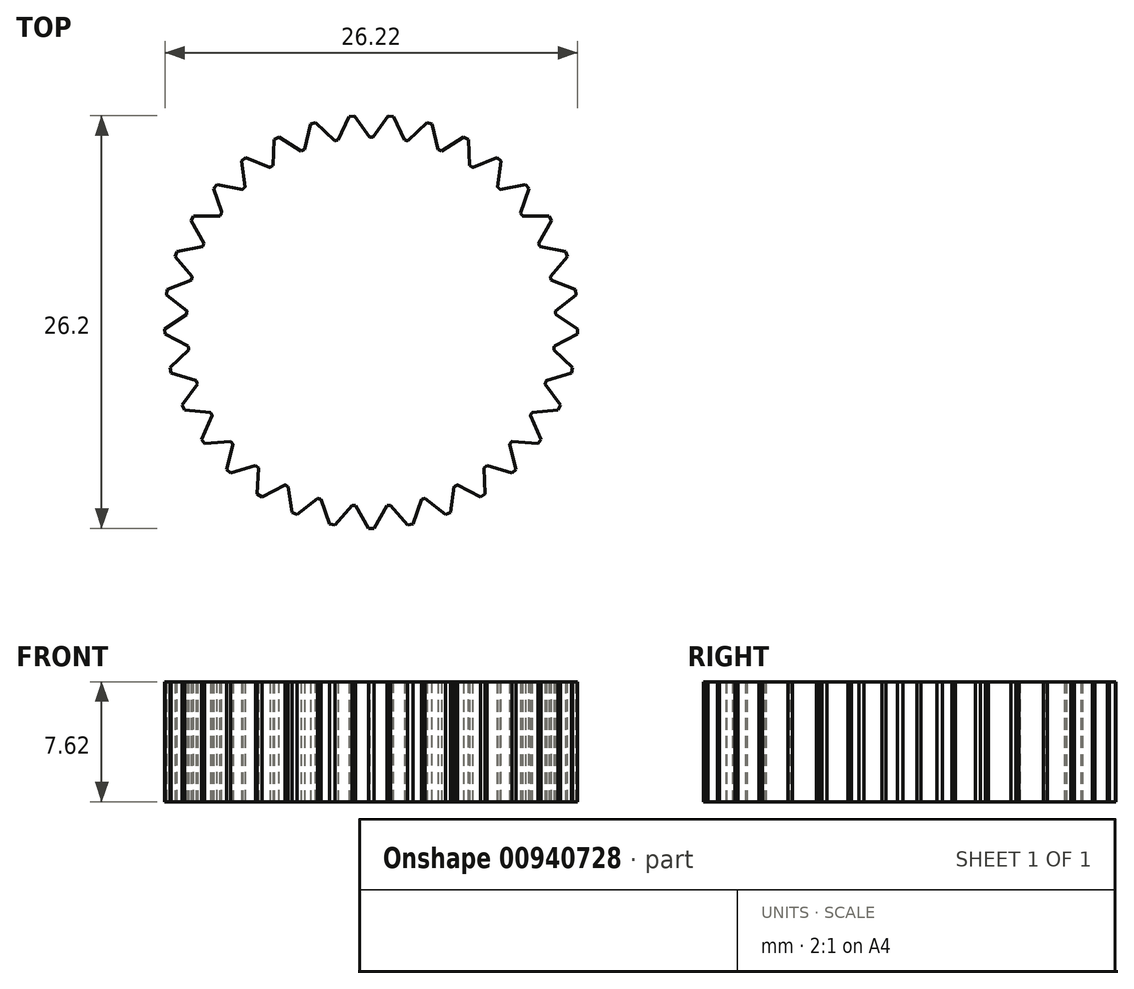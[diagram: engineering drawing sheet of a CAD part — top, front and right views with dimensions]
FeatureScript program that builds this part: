
annotation { "Feature Type Name" : "Feature", "Feature Type Description" : "" }
export const myFeature = defineFeature(function(context is Context, id is Id, definition is map)
    precondition{}
    {
        {
            var Q0;
            Q0=qCreatedBy(makeId("Top.planeOp"),FACE);
            var sketch = newSketch(context, id + "F0", { "sketchPlane" : qUnion([Q0])});
            skCircle(sketch, "E0", {"center": v(0, 0) * mm, "radius": 11.73 * mm});
            skSolve(sketch);
        }
        {
            var Q0;
            Q0 = qSketchRegion(id + "F0", true);
            extrude(context, id + "F1", {"entities" : qUnion([Q0]), "depth" : 7.62 * mm, "offsetDistance" : 25 * mm});
        }
        {
            var Q0;
            Q0=makeQuery(id+"F1.opExtrude","CAP_FACE",FACE,{"disambiguationData":[OSD([sQuery(id+"F0.wireOp",EDGE,"E0")])],"isStart":true});
            var sketch = newSketch(context, id + "F2", { "sketchPlane" : qUnion([Q0])});
            skCircle(sketch, "E1.cCircle", {"center": v(0, 12.26) * mm, "radius": 0.58 * mm, "construction": true});
            skLineSegment(sketch, "E1.0", {"start": v(1, 11.69) * mm, "end": v(-1, 11.69) * mm});
            skLineSegment(sketch, "E1.1", {"start": v(-1, 11.69) * mm, "end": v(0, 13.42) * mm});
            skLineSegment(sketch, "E1.2", {"start": v(0, 13.42) * mm, "end": v(1, 11.69) * mm});
            skPoint(sketch, "E1.0.midPoint", {"position": v(0, 11.69) * mm});
            skLineSegment(sketch, "E2.1.0", {"start": v(-3.2, 11.29) * mm, "end": v(-2.54, 13.18) * mm});
            skLineSegment(sketch, "E2.1.1", {"start": v(-2.54, 13.18) * mm, "end": v(-1.23, 11.66) * mm});
            skLineSegment(sketch, "E2.1.2", {"start": v(-1.23, 11.66) * mm, "end": v(-3.2, 11.29) * mm});
            skLineSegment(sketch, "E2.2.0", {"start": v(-5.27, 10.48) * mm, "end": v(-4.99, 12.46) * mm});
            skLineSegment(sketch, "E2.2.1", {"start": v(-4.99, 12.46) * mm, "end": v(-3.42, 11.22) * mm});
            skLineSegment(sketch, "E2.2.2", {"start": v(-3.42, 11.22) * mm, "end": v(-5.27, 10.48) * mm});
            skLineSegment(sketch, "E2.3.0", {"start": v(-7.16, 9.3) * mm, "end": v(-7.25, 11.29) * mm});
            skLineSegment(sketch, "E2.3.1", {"start": v(-7.25, 11.29) * mm, "end": v(-5.48, 10.37) * mm});
            skLineSegment(sketch, "E2.3.2", {"start": v(-5.48, 10.37) * mm, "end": v(-7.16, 9.3) * mm});
            skLineSegment(sketch, "E2.4.0", {"start": v(-8.79, 7.77) * mm, "end": v(-9.26, 9.71) * mm});
            skLineSegment(sketch, "E2.4.1", {"start": v(-9.26, 9.71) * mm, "end": v(-7.34, 9.15) * mm});
            skLineSegment(sketch, "E2.4.2", {"start": v(-7.34, 9.15) * mm, "end": v(-8.79, 7.77) * mm});
            skLineSegment(sketch, "E2.5.0", {"start": v(-10.1, 5.96) * mm, "end": v(-10.93, 7.78) * mm});
            skLineSegment(sketch, "E2.5.1", {"start": v(-10.93, 7.78) * mm, "end": v(-8.94, 7.6) * mm});
            skLineSegment(sketch, "E2.5.2", {"start": v(-8.94, 7.6) * mm, "end": v(-10.1, 5.96) * mm});
            skLineSegment(sketch, "E2.6.0", {"start": v(-11.05, 3.95) * mm, "end": v(-12.2, 5.57) * mm});
            skLineSegment(sketch, "E2.6.1", {"start": v(-12.2, 5.57) * mm, "end": v(-10.22, 5.76) * mm});
            skLineSegment(sketch, "E2.6.2", {"start": v(-10.22, 5.76) * mm, "end": v(-11.05, 3.95) * mm});
            skLineSegment(sketch, "E2.7.0", {"start": v(-11.6, 1.78) * mm, "end": v(-13.04, 3.16) * mm});
            skLineSegment(sketch, "E2.7.1", {"start": v(-13.04, 3.16) * mm, "end": v(-11.12, 3.73) * mm});
            skLineSegment(sketch, "E2.7.2", {"start": v(-11.12, 3.73) * mm, "end": v(-11.6, 1.78) * mm});
            skLineSegment(sketch, "E2.8.0", {"start": v(-11.72, -0.44) * mm, "end": v(-13.4, 0.64) * mm});
            skLineSegment(sketch, "E2.8.1", {"start": v(-13.4, 0.64) * mm, "end": v(-11.63, 1.55) * mm});
            skLineSegment(sketch, "E2.8.2", {"start": v(-11.63, 1.55) * mm, "end": v(-11.72, -0.44) * mm});
            skLineSegment(sketch, "E2.9.0", {"start": v(-11.43, -2.65) * mm, "end": v(-13.28, -1.9) * mm});
            skLineSegment(sketch, "E2.9.1", {"start": v(-13.28, -1.9) * mm, "end": v(-11.7, -0.67) * mm});
            skLineSegment(sketch, "E2.9.2", {"start": v(-11.7, -0.67) * mm, "end": v(-11.43, -2.65) * mm});
            skLineSegment(sketch, "E2.10.0", {"start": v(-10.72, -4.77) * mm, "end": v(-12.68, -4.39) * mm});
            skLineSegment(sketch, "E2.10.1", {"start": v(-12.68, -4.39) * mm, "end": v(-11.37, -2.88) * mm});
            skLineSegment(sketch, "E2.10.2", {"start": v(-11.37, -2.88) * mm, "end": v(-10.72, -4.77) * mm});
            skLineSegment(sketch, "E2.11.0", {"start": v(-9.62, -6.7) * mm, "end": v(-11.62, -6.7) * mm});
            skLineSegment(sketch, "E2.11.1", {"start": v(-11.62, -6.7) * mm, "end": v(-10.62, -4.98) * mm});
            skLineSegment(sketch, "E2.11.2", {"start": v(-10.62, -4.98) * mm, "end": v(-9.62, -6.7) * mm});
            skLineSegment(sketch, "E2.12.0", {"start": v(-8.18, -8.4) * mm, "end": v(-10.14, -8.79) * mm});
            skLineSegment(sketch, "E2.12.1", {"start": v(-10.14, -8.79) * mm, "end": v(-9.49, -6.9) * mm});
            skLineSegment(sketch, "E2.12.2", {"start": v(-9.49, -6.9) * mm, "end": v(-8.18, -8.4) * mm});
            skLineSegment(sketch, "E2.13.0", {"start": v(-6.44, -9.8) * mm, "end": v(-8.3, -10.55) * mm});
            skLineSegment(sketch, "E2.13.1", {"start": v(-8.3, -10.55) * mm, "end": v(-8.01, -8.57) * mm});
            skLineSegment(sketch, "E2.13.2", {"start": v(-8.01, -8.57) * mm, "end": v(-6.44, -9.8) * mm});
            skLineSegment(sketch, "E2.14.0", {"start": v(-4.47, -10.85) * mm, "end": v(-6.15, -11.93) * mm});
            skLineSegment(sketch, "E2.14.1", {"start": v(-6.15, -11.93) * mm, "end": v(-6.24, -9.93) * mm});
            skLineSegment(sketch, "E2.14.2", {"start": v(-6.24, -9.93) * mm, "end": v(-4.47, -10.85) * mm});
            skLineSegment(sketch, "E2.15.0", {"start": v(-2.33, -11.5) * mm, "end": v(-3.78, -12.88) * mm});
            skLineSegment(sketch, "E2.15.1", {"start": v(-3.78, -12.88) * mm, "end": v(-4.25, -10.93) * mm});
            skLineSegment(sketch, "E2.15.2", {"start": v(-4.25, -10.93) * mm, "end": v(-2.33, -11.5) * mm});
            skLineSegment(sketch, "E2.16.0", {"start": v(-0.12, -11.73) * mm, "end": v(-1.28, -13.36) * mm});
            skLineSegment(sketch, "E2.16.1", {"start": v(-1.28, -13.36) * mm, "end": v(-2.1, -11.54) * mm});
            skLineSegment(sketch, "E2.16.2", {"start": v(-2.1, -11.54) * mm, "end": v(-0.12, -11.73) * mm});
            skLineSegment(sketch, "E2.17.0", {"start": v(2.1, -11.54) * mm, "end": v(1.28, -13.36) * mm});
            skLineSegment(sketch, "E2.17.1", {"start": v(1.28, -13.36) * mm, "end": v(0.12, -11.73) * mm});
            skLineSegment(sketch, "E2.17.2", {"start": v(0.12, -11.73) * mm, "end": v(2.1, -11.54) * mm});
            skLineSegment(sketch, "E2.18.0", {"start": v(4.25, -10.93) * mm, "end": v(3.78, -12.88) * mm});
            skLineSegment(sketch, "E2.18.1", {"start": v(3.78, -12.88) * mm, "end": v(2.33, -11.5) * mm});
            skLineSegment(sketch, "E2.18.2", {"start": v(2.33, -11.5) * mm, "end": v(4.25, -10.93) * mm});
            skLineSegment(sketch, "E2.19.0", {"start": v(6.24, -9.93) * mm, "end": v(6.15, -11.93) * mm});
            skLineSegment(sketch, "E2.19.1", {"start": v(6.15, -11.93) * mm, "end": v(4.47, -10.85) * mm});
            skLineSegment(sketch, "E2.19.2", {"start": v(4.47, -10.85) * mm, "end": v(6.24, -9.93) * mm});
            skLineSegment(sketch, "E2.20.0", {"start": v(8.01, -8.57) * mm, "end": v(8.3, -10.55) * mm});
            skLineSegment(sketch, "E2.20.1", {"start": v(8.3, -10.55) * mm, "end": v(6.44, -9.8) * mm});
            skLineSegment(sketch, "E2.20.2", {"start": v(6.44, -9.8) * mm, "end": v(8.01, -8.57) * mm});
            skLineSegment(sketch, "E2.21.0", {"start": v(9.49, -6.9) * mm, "end": v(10.14, -8.79) * mm});
            skLineSegment(sketch, "E2.21.1", {"start": v(10.14, -8.79) * mm, "end": v(8.18, -8.4) * mm});
            skLineSegment(sketch, "E2.21.2", {"start": v(8.18, -8.4) * mm, "end": v(9.49, -6.9) * mm});
            skLineSegment(sketch, "E2.22.0", {"start": v(10.62, -4.98) * mm, "end": v(11.62, -6.7) * mm});
            skLineSegment(sketch, "E2.22.1", {"start": v(11.62, -6.7) * mm, "end": v(9.62, -6.7) * mm});
            skLineSegment(sketch, "E2.22.2", {"start": v(9.62, -6.7) * mm, "end": v(10.62, -4.98) * mm});
            skLineSegment(sketch, "E2.23.0", {"start": v(11.37, -2.88) * mm, "end": v(12.68, -4.39) * mm});
            skLineSegment(sketch, "E2.23.1", {"start": v(12.68, -4.39) * mm, "end": v(10.72, -4.77) * mm});
            skLineSegment(sketch, "E2.23.2", {"start": v(10.72, -4.77) * mm, "end": v(11.37, -2.88) * mm});
            skPoint(sketch, "E2.center", {"position": v(0, 0) * mm});
            skLineSegment(sketch, "E3.1.24.0", {"start": v(11.7, -0.67) * mm, "end": v(13.28, -1.9) * mm});
            skLineSegment(sketch, "E3.3.24.0", {"start": v(13.28, -1.9) * mm, "end": v(11.43, -2.65) * mm});
            skLineSegment(sketch, "E3.6.24.0", {"start": v(11.43, -2.65) * mm, "end": v(11.7, -0.67) * mm});
            skLineSegment(sketch, "E3.1.25.0", {"start": v(11.63, 1.55) * mm, "end": v(13.4, 0.64) * mm});
            skLineSegment(sketch, "E3.3.25.0", {"start": v(13.4, 0.64) * mm, "end": v(11.72, -0.44) * mm});
            skLineSegment(sketch, "E3.6.25.0", {"start": v(11.72, -0.44) * mm, "end": v(11.63, 1.55) * mm});
            skLineSegment(sketch, "E4.1.26.0", {"start": v(11.12, 3.73) * mm, "end": v(13.04, 3.16) * mm});
            skLineSegment(sketch, "E4.3.26.0", {"start": v(13.04, 3.16) * mm, "end": v(11.6, 1.78) * mm});
            skLineSegment(sketch, "E4.6.26.0", {"start": v(11.6, 1.78) * mm, "end": v(11.12, 3.73) * mm});
            skLineSegment(sketch, "E4.1.27.0", {"start": v(10.22, 5.76) * mm, "end": v(12.2, 5.57) * mm});
            skLineSegment(sketch, "E4.3.27.0", {"start": v(12.2, 5.57) * mm, "end": v(11.05, 3.95) * mm});
            skLineSegment(sketch, "E4.6.27.0", {"start": v(11.05, 3.95) * mm, "end": v(10.22, 5.76) * mm});
            skLineSegment(sketch, "E5.1.28.0", {"start": v(8.94, 7.6) * mm, "end": v(10.93, 7.78) * mm});
            skLineSegment(sketch, "E5.3.28.0", {"start": v(10.93, 7.78) * mm, "end": v(10.1, 5.96) * mm});
            skLineSegment(sketch, "E5.6.28.0", {"start": v(10.1, 5.96) * mm, "end": v(8.94, 7.6) * mm});
            skLineSegment(sketch, "E5.1.29.0", {"start": v(7.34, 9.15) * mm, "end": v(9.26, 9.71) * mm});
            skLineSegment(sketch, "E5.3.29.0", {"start": v(9.26, 9.71) * mm, "end": v(8.79, 7.77) * mm});
            skLineSegment(sketch, "E5.6.29.0", {"start": v(8.79, 7.77) * mm, "end": v(7.34, 9.15) * mm});
            skLineSegment(sketch, "E5.1.30.0", {"start": v(5.48, 10.37) * mm, "end": v(7.25, 11.29) * mm});
            skLineSegment(sketch, "E5.3.30.0", {"start": v(7.25, 11.29) * mm, "end": v(7.16, 9.3) * mm});
            skLineSegment(sketch, "E5.6.30.0", {"start": v(7.16, 9.3) * mm, "end": v(5.48, 10.37) * mm});
            skLineSegment(sketch, "E6.1.31.0", {"start": v(3.42, 11.22) * mm, "end": v(4.99, 12.46) * mm});
            skLineSegment(sketch, "E6.3.31.0", {"start": v(4.99, 12.46) * mm, "end": v(5.27, 10.48) * mm});
            skLineSegment(sketch, "E6.6.31.0", {"start": v(5.27, 10.48) * mm, "end": v(3.42, 11.22) * mm});
            skLineSegment(sketch, "E6.1.32.0", {"start": v(1.23, 11.66) * mm, "end": v(2.54, 13.18) * mm});
            skLineSegment(sketch, "E6.3.32.0", {"start": v(2.54, 13.18) * mm, "end": v(3.2, 11.29) * mm});
            skLineSegment(sketch, "E6.6.32.0", {"start": v(3.2, 11.29) * mm, "end": v(1.23, 11.66) * mm});
            skSolve(sketch);
        }
        {
            var Q0;
            Q0 = qSketchRegion(id + "F2", true);
            var Q1;
            Q1=makeQuery(id+"F1.opExtrude","CAP_FACE",FACE,{"disambiguationData":[OSD([sQuery(id+"F0.wireOp",EDGE,"E0")])],"isStart":false});
            extrude(context, id + "F3", {"entities" : qUnion([Q0]), "operationType" : NewBodyOperationType.ADD, "endBound" : BoundingType.UP_TO_SURFACE, "oppositeDirection" : true, "depth" : 25 * mm, "endBoundEntityFace" : qUnion([Q1]), "offsetDistance" : 25 * mm});
        }
        {
            var Q0;
            Q0=makeQuery(id+"F3.opExtrude","SWEPT_EDGE",EDGE,{"disambiguationData":[OSD([sQuery(id+"F2.wireOp",EDGE,"E2.9.0"),sQuery(id+"F2.wireOp",EDGE,"E2.9.1")])]});
            var Q1;
            Q1=makeQuery(id+"F3.opExtrude","SWEPT_EDGE",EDGE,{"disambiguationData":[OSD([sQuery(id+"F2.wireOp",EDGE,"E2.8.0"),sQuery(id+"F2.wireOp",EDGE,"E2.8.1")])]});
            var Q2;
            Q2=makeQuery(id+"F3.opExtrude","SWEPT_EDGE",EDGE,{"disambiguationData":[OSD([sQuery(id+"F2.wireOp",EDGE,"E2.7.0"),sQuery(id+"F2.wireOp",EDGE,"E2.7.1")])]});
            var Q3;
            Q3=makeQuery(id+"F3.opExtrude","SWEPT_EDGE",EDGE,{"disambiguationData":[OSD([sQuery(id+"F2.wireOp",EDGE,"E2.6.0"),sQuery(id+"F2.wireOp",EDGE,"E2.6.1")])]});
            var Q4;
            Q4=makeQuery(id+"F3.opExtrude","SWEPT_EDGE",EDGE,{"disambiguationData":[OSD([sQuery(id+"F2.wireOp",EDGE,"E2.10.0"),sQuery(id+"F2.wireOp",EDGE,"E2.10.1")])]});
            var Q5;
            Q5=makeQuery(id+"F3.opExtrude","SWEPT_EDGE",EDGE,{"disambiguationData":[OSD([sQuery(id+"F2.wireOp",EDGE,"E2.11.0"),sQuery(id+"F2.wireOp",EDGE,"E2.11.1")])]});
            var Q6;
            Q6=makeQuery(id+"F3.opExtrude","SWEPT_EDGE",EDGE,{"disambiguationData":[OSD([sQuery(id+"F0.wireOp",EDGE,"E0"),sQuery(id+"F2.wireOp",EDGE,"E2.12.1"),sQuery(id+"F2.wireOp",EDGE,"E2.12.2")])]});
            var Q7;
            Q7=makeQuery(id+"F3.opExtrude","SWEPT_EDGE",EDGE,{"disambiguationData":[OSD([sQuery(id+"F2.wireOp",EDGE,"E2.12.0"),sQuery(id+"F2.wireOp",EDGE,"E2.12.1")])]});
            var Q8;
            Q8=makeQuery(id+"F3.opExtrude","SWEPT_EDGE",EDGE,{"disambiguationData":[OSD([sQuery(id+"F2.wireOp",EDGE,"E2.13.0"),sQuery(id+"F2.wireOp",EDGE,"E2.13.1")])]});
            var Q9;
            Q9=makeQuery(id+"F3.opExtrude","SWEPT_EDGE",EDGE,{"disambiguationData":[OSD([sQuery(id+"F2.wireOp",EDGE,"E2.14.0"),sQuery(id+"F2.wireOp",EDGE,"E2.14.1")])]});
            var Q10;
            Q10=makeQuery(id+"F3.opExtrude","SWEPT_EDGE",EDGE,{"disambiguationData":[OSD([sQuery(id+"F2.wireOp",EDGE,"E2.15.0"),sQuery(id+"F2.wireOp",EDGE,"E2.15.1")])]});
            var Q11;
            Q11=makeQuery(id+"F3.opExtrude","SWEPT_EDGE",EDGE,{"disambiguationData":[OSD([sQuery(id+"F2.wireOp",EDGE,"E2.16.0"),sQuery(id+"F2.wireOp",EDGE,"E2.16.1")])]});
            var Q12;
            Q12=makeQuery(id+"F3.opExtrude","SWEPT_EDGE",EDGE,{"disambiguationData":[OSD([sQuery(id+"F2.wireOp",EDGE,"E2.17.0"),sQuery(id+"F2.wireOp",EDGE,"E2.17.1")])]});
            var Q13;
            Q13=makeQuery(id+"F3.opExtrude","SWEPT_EDGE",EDGE,{"disambiguationData":[OSD([sQuery(id+"F2.wireOp",EDGE,"E2.18.0"),sQuery(id+"F2.wireOp",EDGE,"E2.18.1")])]});
            var Q14;
            Q14=makeQuery(id+"F3.opExtrude","SWEPT_EDGE",EDGE,{"disambiguationData":[OSD([sQuery(id+"F2.wireOp",EDGE,"E2.19.0"),sQuery(id+"F2.wireOp",EDGE,"E2.19.1")])]});
            var Q15;
            Q15=makeQuery(id+"F3.opExtrude","SWEPT_EDGE",EDGE,{"disambiguationData":[OSD([sQuery(id+"F2.wireOp",EDGE,"E2.20.0"),sQuery(id+"F2.wireOp",EDGE,"E2.20.1")])]});
            var Q16;
            Q16=makeQuery(id+"F3.opExtrude","SWEPT_EDGE",EDGE,{"disambiguationData":[OSD([sQuery(id+"F2.wireOp",EDGE,"E2.21.0"),sQuery(id+"F2.wireOp",EDGE,"E2.21.1")])]});
            var Q17;
            Q17=makeQuery(id+"F3.opExtrude","SWEPT_EDGE",EDGE,{"disambiguationData":[OSD([sQuery(id+"F2.wireOp",EDGE,"E2.22.0"),sQuery(id+"F2.wireOp",EDGE,"E2.22.1")])]});
            var Q18;
            Q18=makeQuery(id+"F3.opExtrude","SWEPT_EDGE",EDGE,{"disambiguationData":[OSD([sQuery(id+"F2.wireOp",EDGE,"E2.23.0"),sQuery(id+"F2.wireOp",EDGE,"E2.23.1")])]});
            var Q19;
            Q19=makeQuery(id+"F3.opExtrude","SWEPT_EDGE",EDGE,{"disambiguationData":[OSD([sQuery(id+"F2.wireOp",EDGE,"E3.1.24.0"),sQuery(id+"F2.wireOp",EDGE,"E3.3.24.0")])]});
            var Q20;
            Q20=makeQuery(id+"F3.opExtrude","SWEPT_EDGE",EDGE,{"disambiguationData":[OSD([sQuery(id+"F2.wireOp",EDGE,"E3.1.25.0"),sQuery(id+"F2.wireOp",EDGE,"E3.3.25.0")])]});
            var Q21;
            Q21=makeQuery(id+"F3.opExtrude","SWEPT_EDGE",EDGE,{"disambiguationData":[OSD([sQuery(id+"F2.wireOp",EDGE,"E4.1.26.0"),sQuery(id+"F2.wireOp",EDGE,"E4.3.26.0")])]});
            var Q22;
            Q22=makeQuery(id+"F3.opExtrude","SWEPT_EDGE",EDGE,{"disambiguationData":[OSD([sQuery(id+"F2.wireOp",EDGE,"E4.1.27.0"),sQuery(id+"F2.wireOp",EDGE,"E4.3.27.0")])]});
            var Q23;
            Q23=makeQuery(id+"F3.opExtrude","SWEPT_EDGE",EDGE,{"disambiguationData":[OSD([sQuery(id+"F2.wireOp",EDGE,"E5.1.28.0"),sQuery(id+"F2.wireOp",EDGE,"E5.3.28.0")])]});
            var Q24;
            Q24=makeQuery(id+"F3.opExtrude","SWEPT_EDGE",EDGE,{"disambiguationData":[OSD([sQuery(id+"F2.wireOp",EDGE,"E5.1.29.0"),sQuery(id+"F2.wireOp",EDGE,"E5.3.29.0")])]});
            var Q25;
            Q25=makeQuery(id+"F3.opExtrude","SWEPT_EDGE",EDGE,{"disambiguationData":[OSD([sQuery(id+"F2.wireOp",EDGE,"E5.1.30.0"),sQuery(id+"F2.wireOp",EDGE,"E5.3.30.0")])]});
            var Q26;
            Q26=makeQuery(id+"F3.opExtrude","SWEPT_EDGE",EDGE,{"disambiguationData":[OSD([sQuery(id+"F2.wireOp",EDGE,"E6.1.31.0"),sQuery(id+"F2.wireOp",EDGE,"E6.3.31.0")])]});
            var Q27;
            Q27=makeQuery(id+"F3.opExtrude","SWEPT_EDGE",EDGE,{"disambiguationData":[OSD([sQuery(id+"F2.wireOp",EDGE,"E6.1.32.0"),sQuery(id+"F2.wireOp",EDGE,"E6.3.32.0")])]});
            var Q28;
            Q28=makeQuery(id+"F3.opExtrude","SWEPT_EDGE",EDGE,{"disambiguationData":[OSD([sQuery(id+"F2.wireOp",EDGE,"E1.1"),sQuery(id+"F2.wireOp",EDGE,"E1.2")])]});
            var Q29;
            Q29=makeQuery(id+"F3.opExtrude","SWEPT_EDGE",EDGE,{"disambiguationData":[OSD([sQuery(id+"F2.wireOp",EDGE,"E2.1.0"),sQuery(id+"F2.wireOp",EDGE,"E2.1.1")])]});
            var Q30;
            Q30=makeQuery(id+"F3.opExtrude","SWEPT_EDGE",EDGE,{"disambiguationData":[OSD([sQuery(id+"F2.wireOp",EDGE,"E2.2.0"),sQuery(id+"F2.wireOp",EDGE,"E2.2.1")])]});
            var Q31;
            Q31=makeQuery(id+"F3.opExtrude","SWEPT_EDGE",EDGE,{"disambiguationData":[OSD([sQuery(id+"F2.wireOp",EDGE,"E2.3.0"),sQuery(id+"F2.wireOp",EDGE,"E2.3.1")])]});
            var Q32;
            Q32=makeQuery(id+"F3.opExtrude","SWEPT_EDGE",EDGE,{"disambiguationData":[OSD([sQuery(id+"F2.wireOp",EDGE,"E2.4.0"),sQuery(id+"F2.wireOp",EDGE,"E2.4.1")])]});
            var Q33;
            Q33=makeQuery(id+"F3.opExtrude","SWEPT_EDGE",EDGE,{"disambiguationData":[OSD([sQuery(id+"F2.wireOp",EDGE,"E2.5.0"),sQuery(id+"F2.wireOp",EDGE,"E2.5.1")])]});
            chamfer(context, id + "F4", {"entities" : qUnion([Q0, Q1, Q2, Q3, Q4, Q5, Q6, Q7, Q8, Q9, Q10, Q11, Q12, Q13, Q14, Q15, Q16, Q17, Q18, Q19, Q20, Q21, Q22, Q23, Q24, Q25, Q26, Q27, Q28, Q29, Q30, Q31, Q32, Q33]), "width" : .2 * mm, "tangentPropagation" : true});
        }
    });
